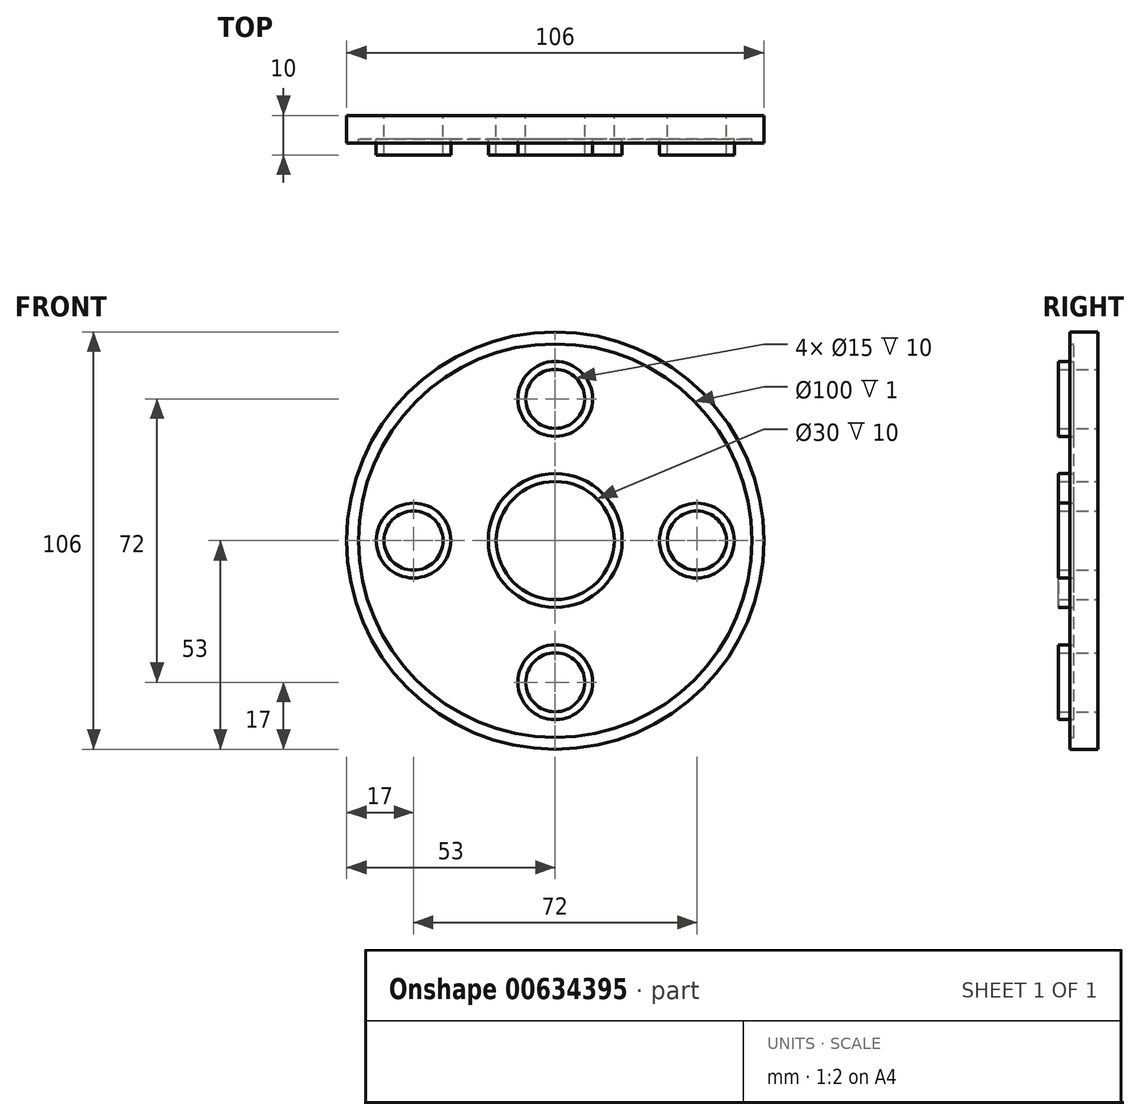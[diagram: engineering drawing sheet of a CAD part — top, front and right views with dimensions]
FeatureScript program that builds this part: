
annotation { "Feature Type Name" : "Feature", "Feature Type Description" : "" }
export const myFeature = defineFeature(function(context is Context, id is Id, definition is map)
    precondition{}
    {
        {
            var Q0;
            Q0=qCreatedBy(makeId("Front.planeOp"),FACE);
            var sketch = newSketch(context, id + "F0", { "sketchPlane" : qUnion([Q0])});
            skCircle(sketch, "E0", {"center": v(0, 0) * mm, "radius": 15 * mm});
            skCircle(sketch, "E1", {"center": v(0, 0) * mm, "radius": 17 * mm});
            skCircle(sketch, "E2", {"center": v(-36, 0) * mm, "radius": 7.5 * mm});
            skCircle(sketch, "E3", {"center": v(-36, 0) * mm, "radius": 9.5 * mm});
            skCircle(sketch, "E4", {"center": v(0, 0) * mm, "radius": 50 * mm});
            skCircle(sketch, "E5", {"center": v(0, 0) * mm, "radius": 53 * mm});
            skCircle(sketch, "E6", {"center": v(0, 36) * mm, "radius": 7.5 * mm});
            skCircle(sketch, "E7", {"center": v(0, 36) * mm, "radius": 9.5 * mm});
            skCircle(sketch, "E8", {"center": v(36, 0) * mm, "radius": 7.5 * mm});
            skCircle(sketch, "E9", {"center": v(36, 0) * mm, "radius": 9.5 * mm});
            skCircle(sketch, "E10", {"center": v(0, -36) * mm, "radius": 7.5 * mm});
            skCircle(sketch, "E11", {"center": v(0, -36) * mm, "radius": 9.5 * mm});
            skSolve(sketch);
        }
        {
            var Q0;
            Q0=makeQuery(id+"F0.imprint","IMPRINT",FACE,{"disambiguationData":[TD([[makeQuery(id+"F0.imprint","IMPRINT",EDGE,{"derivedFrom":sQuery(id+"F0.wireOp",EDGE,"E4")}),-1.0]])]});
            extrude(context, id + "F1", {"entities" : qUnion([Q0]), "depth" : 7 * mm, "offsetDistance" : 25 * mm});
        }
        {
            var Q0;
            Q0=makeQuery(id+"F0.imprint","IMPRINT",FACE,{"disambiguationData":[TD([[makeQuery(id+"F0.imprint","IMPRINT",EDGE,{"derivedFrom":sQuery(id+"F0.wireOp",EDGE,"E1")}),-1.0]])]});
            extrude(context, id + "F2", {"entities" : qUnion([Q0]), "operationType" : NewBodyOperationType.ADD, "depth" : 6 * mm, "offsetDistance" : 25 * mm});
        }
        {
            var Q0;
            Q0=makeQuery(id+"F0.imprint","IMPRINT",FACE,{"disambiguationData":[TD([[makeQuery(id+"F0.imprint","IMPRINT",EDGE,{"derivedFrom":sQuery(id+"F0.wireOp",EDGE,"E8")}),-1.0]])]});
            var Q1;
            Q1=makeQuery(id+"F0.imprint","IMPRINT",FACE,{"disambiguationData":[TD([[makeQuery(id+"F0.imprint","IMPRINT",EDGE,{"derivedFrom":sQuery(id+"F0.wireOp",EDGE,"E0")}),-1.0]])]});
            var Q2;
            Q2=makeQuery(id+"F0.imprint","IMPRINT",FACE,{"disambiguationData":[TD([[makeQuery(id+"F0.imprint","IMPRINT",EDGE,{"derivedFrom":sQuery(id+"F0.wireOp",EDGE,"E6")}),-1.0]])]});
            var Q3;
            Q3=makeQuery(id+"F0.imprint","IMPRINT",FACE,{"disambiguationData":[TD([[makeQuery(id+"F0.imprint","IMPRINT",EDGE,{"derivedFrom":sQuery(id+"F0.wireOp",EDGE,"E2")}),-1.0]])]});
            var Q4;
            Q4=makeQuery(id+"F0.imprint","IMPRINT",FACE,{"disambiguationData":[TD([[makeQuery(id+"F0.imprint","IMPRINT",EDGE,{"derivedFrom":sQuery(id+"F0.wireOp",EDGE,"E10")}),-1.0]])]});
            extrude(context, id + "F3", {"entities" : qUnion([Q0, Q1, Q2, Q3, Q4]), "operationType" : NewBodyOperationType.ADD, "depth" : 10 * mm, "offsetDistance" : 25 * mm});
        }
    });
